# Revit family: Sanitary_Installation-Systems_DURAVIT-AG_WD1030-Installation-element-wet-installa_NEW
name_source: partatom
category: Plumbing Fixtures
revit_build: Autodesk Revit 2018 (Build: 20170223_1515(x64)
units: mm (PartAtom-declared; Revit-internal decimal feet)

## family parameters
Cut with Voids When Loaded = No
Host = Face
OmniClass Number = 23.31.19.00
OmniClass Title = Toilets
Part Type = Normal
Room Calculation Point = No
Round Connector Dimension = Use Diameter
Shared = No

## types (1)
- WD1030 Installation element wet installation for WC - WD1030000000
    Always visible = Yes
    Connector Description = Water Inlet 38.1 mm
    Default Elevation = 0 mm  [stored 0 ft]
    Depth = 80 mm  [stored 0.262467 ft]
    Description = Comes partly assembled
For wet installation
Individually adjustable flush intensity
Large flush water volume: 6 litres
Minimum flush water required: just 3 litres
Water-saving dual flush: small or large flushes can be selected as required
    Diameter = 38
    Edition number = 1
    Height = 912 mm  [stored 2.99213 ft]
    IFC Classification = Pipe Fitting
    Manufacturer = Duravit
    Manufacturer name = DURAVIT AG
    Masterformat 2014 Code = 22 40 00
    Masterformat 2014 Description = Plumbing Fixtures
    Material 1 = Duravit - Metal - Steel
    Material 2 = Duravit - Plastic - Black Matt
    Material 3 = Duravit - Plastic - Orange
    Material 4 = Duravit - Plastic - White
    Material main = Steel
    Model = WD1030 Installation element wet installation for WC
    NBS Reference Code = 35-65-90
    NBS Reference Description = Toilet Systems
    OmniClass Code = 23-31 19 00
    OmniClass Description = Toilets
    Product Guid = 9680cd69-b299-4272-89e0-fd0f399dd914
    Product SKU = Installation-element-wet-installation-for-WC-WD1030
    Product data url = https://bimobject.com
    Product name = WD1030 Installation element wet installation for WC
    Product url = https://duravit-public-assets.s3.eu-central-1.amazonaws.com
    QR code = https://bimobject.com
    UNSPSC Code = 301815
    URL = http://pro.duravit.com
    Uniclass 1.4 Code = L7216
    Uniclass 1.4 Description = Toilets
    Uniclass 2.0 Code = SS-35-65-90
    Uniclass 2.0 Description = Toilet Systems
    Uniclass 2015 Code = Pr_40_20_93_62
    Uniclass 2015 Name = Pre-plumbed installation frames
    Uniformat II Code = D2030
    Uniformat II Description = Sanitary Waste
    Weight = 5.70 kg
    Width = 422 mm  [stored 1.38451 ft]
    Youtube clip = https://duravit-public-assets.s3.eu-central-1.amazonaws.com

note: [stored X ft] marks values corroborated as IEEE doubles in the binary element streams (Revit-internal decimal feet)

## geometry (parser evidence)
native form markers: Sweep x2
no freeform markers — native parametric forms only
